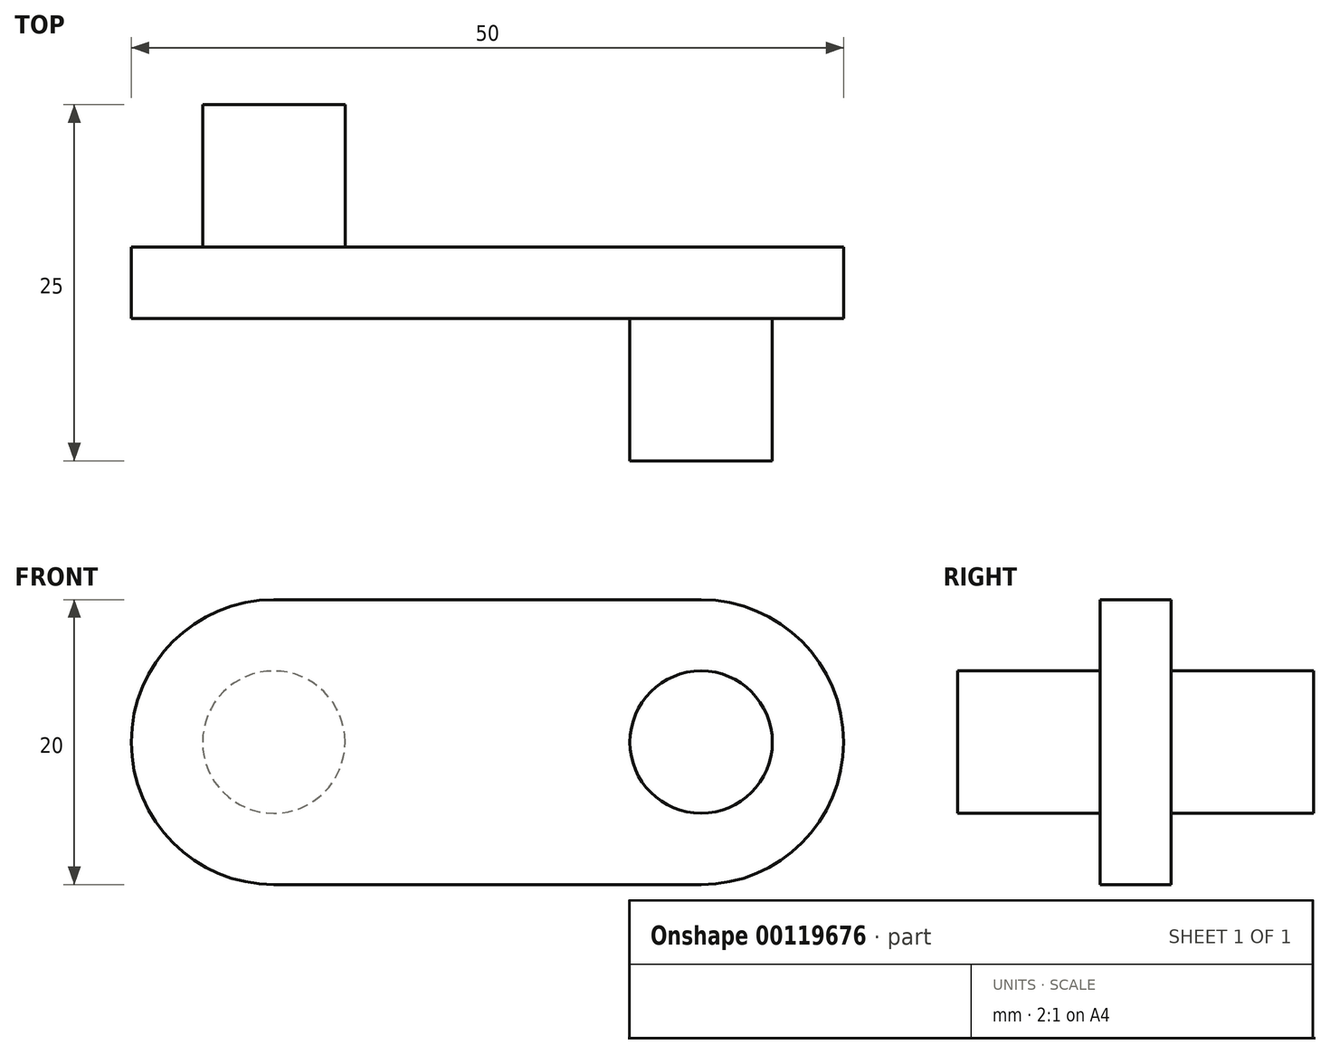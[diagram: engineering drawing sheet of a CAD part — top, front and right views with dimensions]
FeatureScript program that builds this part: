
annotation { "Feature Type Name" : "Feature", "Feature Type Description" : "" }
export const myFeature = defineFeature(function(context is Context, id is Id, definition is map)
    precondition{}
    {
        {
            var Q0;
            Q0=qCreatedBy(makeId("Front.planeOp"),FACE);
            var sketch = newSketch(context, id + "F0", { "sketchPlane" : qUnion([Q0])});
            skArc(sketch, "E0", {"start": v(0, 10) * mm, "mid": v(-10, 0) * mm, "end": v(0, -10) * mm});
            skLineSegment(sketch, "E1", {"start": v(0, 10) * mm, "end": v(30, 10) * mm});
            skLineSegment(sketch, "E2", {"start": v(0, -10) * mm, "end": v(30, -10) * mm});
            skArc(sketch, "E3", {"start": v(30, 10) * mm, "mid": v(40, 0) * mm, "end": v(30, -10) * mm});
            skSolve(sketch);
        }
        {
            var Q0;
            Q0 = qSketchRegion(id + "F0", true);
            extrude(context, id + "F1", {"entities" : qUnion([Q0]), "endBound" : BoundingType.SYMMETRIC, "depth" : 5 * mm});
        }
        {
            var Q0;
            Q0=makeQuery(id+"F1.opExtrude","CAP_FACE",FACE,{"disambiguationData":[OSD([sQuery(id+"F0.wireOp",EDGE,"E0"),sQuery(id+"F0.wireOp",EDGE,"E1"),sQuery(id+"F0.wireOp",EDGE,"E2"),sQuery(id+"F0.wireOp",EDGE,"E3")])],"isStart":false});
            var sketch = newSketch(context, id + "F2", { "sketchPlane" : qUnion([Q0])});
            skCircle(sketch, "E4", {"center": v(30, 0) * mm, "radius": 5 * mm});
            skSolve(sketch);
        }
        {
            var Q0;
            Q0 = qSketchRegion(id + "F2", true);
            extrude(context, id + "F3", {"entities" : qUnion([Q0]), "operationType" : NewBodyOperationType.ADD, "depth" : 10 * mm});
        }
        {
            var Q0;
            Q0=makeQuery(id+"F1.opExtrude","CAP_FACE",FACE,{"disambiguationData":[OSD([sQuery(id+"F0.wireOp",EDGE,"E0"),sQuery(id+"F0.wireOp",EDGE,"E1"),sQuery(id+"F0.wireOp",EDGE,"E2"),sQuery(id+"F0.wireOp",EDGE,"E3")])],"isStart":true});
            var sketch = newSketch(context, id + "F4", { "sketchPlane" : qUnion([Q0])});
            skCircle(sketch, "E5", {"center": v(0, 0) * mm, "radius": 5 * mm});
            skSolve(sketch);
        }
        {
            var Q0;
            Q0 = qSketchRegion(id + "F4", true);
            extrude(context, id + "F5", {"entities" : qUnion([Q0]), "operationType" : NewBodyOperationType.ADD, "depth" : 10 * mm});
        }
    });
